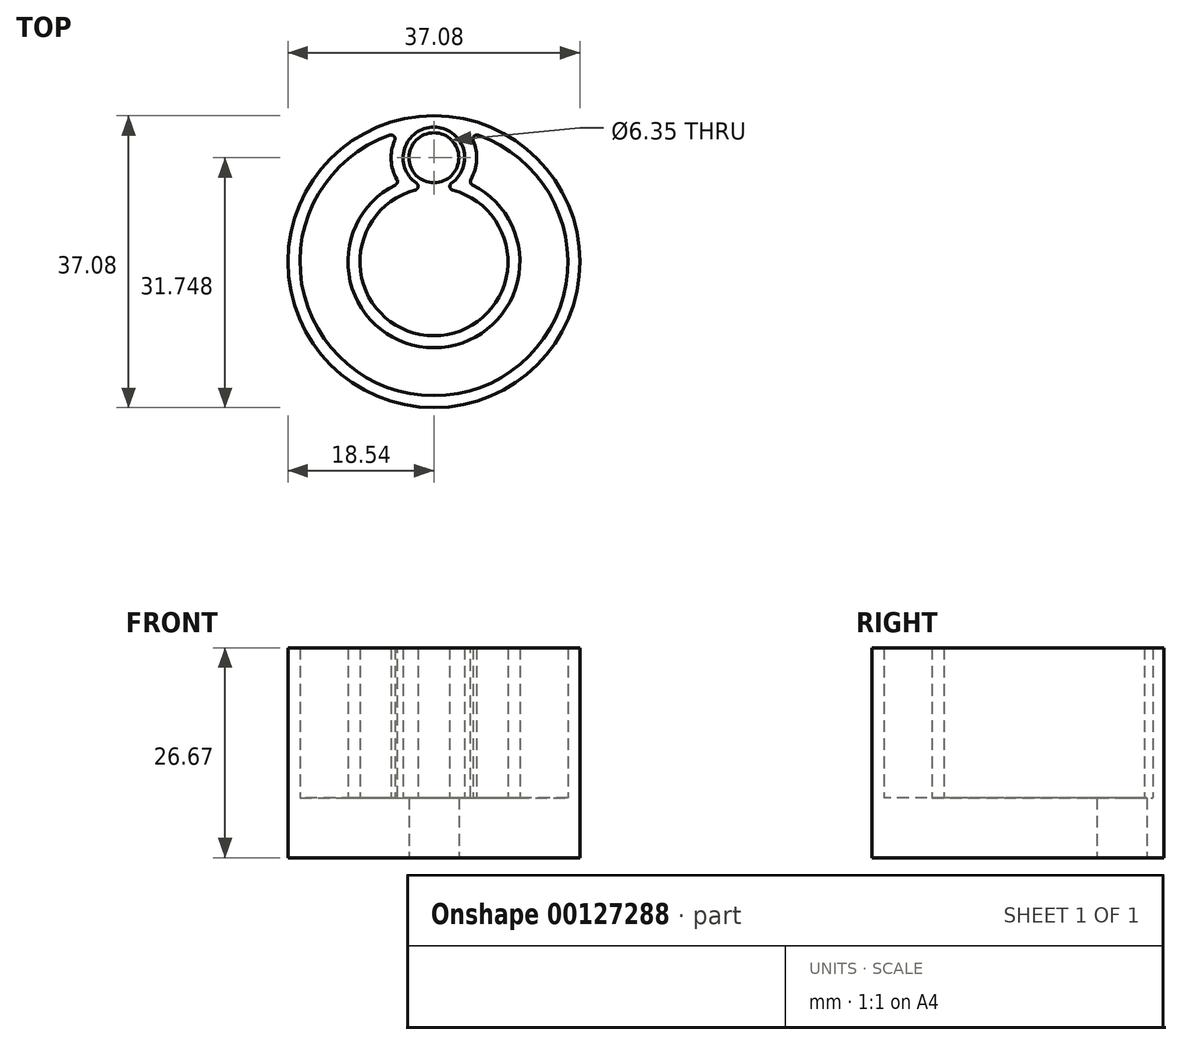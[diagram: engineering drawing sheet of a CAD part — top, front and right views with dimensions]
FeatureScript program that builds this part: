
annotation { "Feature Type Name" : "Feature", "Feature Type Description" : "" }
export const myFeature = defineFeature(function(context is Context, id is Id, definition is map)
    precondition{}
    {
        {
            var Q0;
            Q0=qCreatedBy(makeId("Top.planeOp"),FACE);
            var sketch = newSketch(context, id + "F0", { "sketchPlane" : qUnion([Q0])});
            skCircle(sketch, "E0", {"center": v(0, 0) * mm, "radius": 18.54 * mm});
            skCircle(sketch, "E1", {"center": v(0, 0) * mm, "radius": 17.02 * mm, "construction": true});
            skLineSegment(sketch, "E2", {"start": v(17.02, 0) * mm, "end": v(18.54, 0) * mm, "construction": true});
            skCircle(sketch, "E3", {"center": v(0, 0) * mm, "radius": 9.4 * mm, "construction": true});
            skCircle(sketch, "E4", {"center": v(0, 13.2) * mm, "radius": 3.81 * mm, "construction": true});
            skCircle(sketch, "E5", {"center": v(0, 13.2) * mm, "radius": 3.18 * mm});
            skSolve(sketch);
        }
        {
            var Q0;
            Q0 = qSketchRegion(id + "F0", true);
            extrude(context, id + "F1", {"entities" : qUnion([Q0]), "depth" : 7.62 * mm});
        }
        {
            var Q0;
            Q0=makeQuery(id+"F1.opExtrude","CAP_FACE",FACE,{"disambiguationData":[OSD([sQuery(id+"F0.wireOp",EDGE,"E0"),sQuery(id+"F0.wireOp",EDGE,"E5")])],"isStart":false});
            var sketch = newSketch(context, id + "F2", { "sketchPlane" : qUnion([Q0])});
            skCircle(sketch, "E6", {"center": v(0, 0) * mm, "radius": 18.54 * mm});
            skArc(sketch, "E7", {"start": v(-0.75, 9.37) * mm, "mid": v(0, 9.3) * mm, "end": v(0.75, 9.37) * mm, "construction": true});
            skArc(sketch, "E8", {"start": v(0.75, 9.37) * mm, "mid": v(0, 17.12) * mm, "end": v(-0.75, 9.37) * mm});
            skArc(sketch, "E9", {"start": v(0.75, 9.37) * mm, "mid": v(0, 9.4) * mm, "end": v(-0.75, 9.37) * mm, "construction": true});
            skArc(sketch, "E10", {"start": v(-0.75, 9.37) * mm, "mid": v(0, -9.4) * mm, "end": v(0.75, 9.37) * mm});
            skLineSegment(sketch, "E11", {"start": v(-0.75, 9.37) * mm, "end": v(0.75, 9.37) * mm, "construction": true});
            skPoint(sketch, "E12", {"position": v(0, 9.37) * mm});
            skArc(sketch, "E13", {"start": v(-4.39, 10) * mm, "mid": v(0, -10.92) * mm, "end": v(4.39, 10) * mm});
            skArc(sketch, "E14", {"start": v(4.39, 10) * mm, "mid": v(0, 10.92) * mm, "end": v(-4.39, 10) * mm, "construction": true});
            skArc(sketch, "E15", {"start": v(-4.36, 16.45) * mm, "mid": v(0, -17.02) * mm, "end": v(4.36, 16.45) * mm});
            skArc(sketch, "E16", {"start": v(4.36, 16.45) * mm, "mid": v(0, 17.02) * mm, "end": v(-4.36, 16.45) * mm, "construction": true});
            skArc(sketch, "E17", {"start": v(-4.36, 16.45) * mm, "mid": v(-5.44, 13.23) * mm, "end": v(-4.39, 10) * mm});
            skArc(sketch, "E18", {"start": v(4.39, 10) * mm, "mid": v(5.44, 13.23) * mm, "end": v(4.36, 16.45) * mm});
            skLineSegment(sketch, "E19", {"start": v(9.4, 0) * mm, "end": v(10.92, 0) * mm, "construction": true});
            skSolve(sketch);
        }
        {
            var Q0;
            Q0 = qSketchRegion(id + "F2", true);
            extrude(context, id + "F3", {"entities" : qUnion([Q0]), "operationType" : NewBodyOperationType.ADD, "depth" : 19.05 * mm});
        }
        {
            var Q0;
            {var subQ0=sQuery(id+"F2.wireOp",EDGE,"E10");var subQ1=sQuery(id+"F2.wireOp",EDGE,"E8");Q0=makeQuery(id+"F3.opExtrude","SWEPT_EDGE",EDGE,{"disambiguationData":[OSD([subQ1,subQ0]),TDD([makeQuery(id+"F2.imprint","INTERSECT",VERTEX,{"disambiguationData":[OD(1.0)],"derivedFrom":[subQ1,subQ0]})])]});}
            var Q1;
            {var subQ0=sQuery(id+"F2.wireOp",EDGE,"E10");var subQ1=sQuery(id+"F2.wireOp",EDGE,"E8");Q1=makeQuery(id+"F3.opExtrude","SWEPT_EDGE",EDGE,{"disambiguationData":[OSD([subQ1,subQ0]),TDD([makeQuery(id+"F2.imprint","INTERSECT",VERTEX,{"disambiguationData":[OD(0.0)],"derivedFrom":[subQ1,subQ0]})])]});}
            var Q2;
            Q2=makeQuery(id+"F3.opExtrude","SWEPT_EDGE",EDGE,{"disambiguationData":[OSD([sQuery(id+"F2.wireOp",EDGE,"E13"),sQuery(id+"F2.wireOp",EDGE,"E18")])]});
            var Q3;
            Q3=makeQuery(id+"F3.opExtrude","SWEPT_EDGE",EDGE,{"disambiguationData":[OSD([sQuery(id+"F2.wireOp",EDGE,"E15"),sQuery(id+"F2.wireOp",EDGE,"E18")])]});
            var Q4;
            Q4=makeQuery(id+"F3.opExtrude","SWEPT_EDGE",EDGE,{"disambiguationData":[OSD([sQuery(id+"F2.wireOp",EDGE,"E13"),sQuery(id+"F2.wireOp",EDGE,"E17")])]});
            var Q5;
            Q5=makeQuery(id+"F3.opExtrude","SWEPT_EDGE",EDGE,{"disambiguationData":[OSD([sQuery(id+"F2.wireOp",EDGE,"E15"),sQuery(id+"F2.wireOp",EDGE,"E17")])]});
            fillet(context, id + "F4", {"entities" : qUnion([Q0, Q1, Q2, Q3, Q4, Q5]), "radius" : 0.5 * mm, "tangentPropagation" : true, "allowEdgeOverflow" : false});
        }
    });
